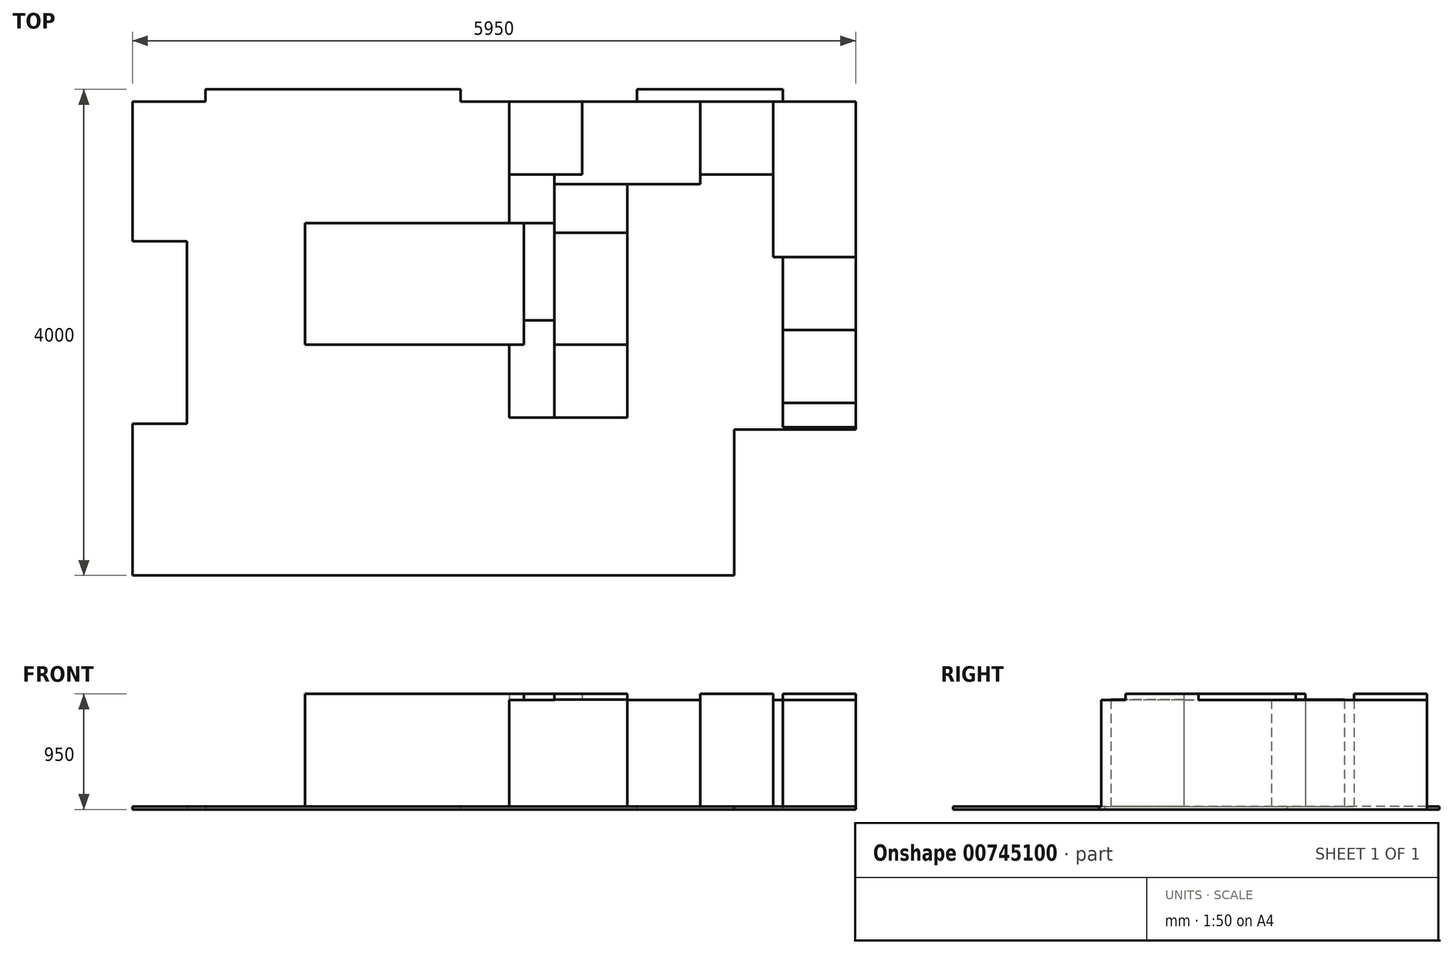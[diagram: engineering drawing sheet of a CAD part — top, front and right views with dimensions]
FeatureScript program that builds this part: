
annotation { "Feature Type Name" : "Feature", "Feature Type Description" : "" }
export const myFeature = defineFeature(function(context is Context, id is Id, definition is map)
    precondition{}
    {
        {
            var Q0;
            Q0=qCreatedBy(makeId("Top.planeOp"),FACE);
            var sketch = newSketch(context, id + "F0", { "sketchPlane" : qUnion([Q0])});
            skLineSegment(sketch, "E0.bottom", {"start": v(0, 0) * mm, "end": v(-1000, 0) * mm});
            skLineSegment(sketch, "E0.top", {"start": v(0, 2700) * mm, "end": v(-600, 2700) * mm});
            skLineSegment(sketch, "E0.left", {"start": v(0, 0) * mm, "end": v(0, 2700) * mm});
            skLineSegment(sketch, "E1.top", {"start": v(-1800, 2800) * mm, "end": v(-600, 2800) * mm});
            skLineSegment(sketch, "E1.left", {"start": v(-1800, 2700) * mm, "end": v(-1800, 2800) * mm});
            skLineSegment(sketch, "E1.right", {"start": v(-600, 2700) * mm, "end": v(-600, 2800) * mm});
            skLineSegment(sketch, "E2.top", {"start": v(-5950, -1200) * mm, "end": v(-1000, -1200) * mm});
            skLineSegment(sketch, "E2.right", {"start": v(-1000, 0) * mm, "end": v(-1000, -1200) * mm});
            skLineSegment(sketch, "E3", {"start": v(-5950, 2700) * mm, "end": v(-5950, 1550) * mm});
            skLineSegment(sketch, "E4.trimOffspring", {"start": v(-1800, 2700) * mm, "end": v(-3250, 2700) * mm});
            skLineSegment(sketch, "E5.top", {"start": v(-5350, 2800) * mm, "end": v(-3250, 2800) * mm});
            skLineSegment(sketch, "E5.left", {"start": v(-5350, 2700) * mm, "end": v(-5350, 2800) * mm});
            skLineSegment(sketch, "E5.right", {"start": v(-3250, 2700) * mm, "end": v(-3250, 2800) * mm});
            skLineSegment(sketch, "E6.trimOffspring", {"start": v(-5350, 2700) * mm, "end": v(-5950, 2700) * mm});
            skLineSegment(sketch, "E7", {"start": v(-5950, 1550) * mm, "end": v(-5500, 1550) * mm});
            skLineSegment(sketch, "E8", {"start": v(-5500, 1550) * mm, "end": v(-5500, 50) * mm});
            skLineSegment(sketch, "E9", {"start": v(-5500, 50) * mm, "end": v(-5950, 50) * mm});
            skLineSegment(sketch, "E10.trimOffspring", {"start": v(-5950, 50) * mm, "end": v(-5950, -1200) * mm});
            skSolve(sketch);
        }
        {
            var Q0;
            Q0=makeQuery(id+"F0.imprint","IMPRINT",FACE,{"disambiguationData":[TD([[makeQuery(id+"F0.imprint","IMPRINT",EDGE,{"derivedFrom":sQuery(id+"F0.wireOp",EDGE,"E0.bottom")}),-1.0]])]});
            extrude(context, id + "F1", {"entities" : qUnion([Q0]), "depth" : 25 * mm, "offsetDistance" : 25 * mm});
        }
        {
            var Q0;
            Q0=qCreatedBy(makeId("Top.planeOp"),FACE);
            var sketch = newSketch(context, id + "F2", { "sketchPlane" : qUnion([Q0])});
            skLineSegment(sketch, "E11.bottom", {"start": v(0, 2700) * mm, "end": v(-680, 2700) * mm});
            skLineSegment(sketch, "E11.top", {"start": v(0, 1420) * mm, "end": v(-680, 1420) * mm});
            skLineSegment(sketch, "E11.left", {"start": v(0, 2700) * mm, "end": v(0, 1420) * mm});
            skLineSegment(sketch, "E11.right", {"start": v(-680, 2700) * mm, "end": v(-680, 1420) * mm});
            skLineSegment(sketch, "E12.bottom", {"start": v(0, 1420) * mm, "end": v(-600, 1420) * mm});
            skLineSegment(sketch, "E12.top", {"start": v(0, 820) * mm, "end": v(-600, 820) * mm});
            skLineSegment(sketch, "E12.left", {"start": v(0, 1420) * mm, "end": v(0, 820) * mm});
            skLineSegment(sketch, "E12.right", {"start": v(-600, 1420) * mm, "end": v(-600, 820) * mm});
            skLineSegment(sketch, "E13.top", {"start": v(0, 220) * mm, "end": v(-600, 220) * mm});
            skLineSegment(sketch, "E13.left", {"start": v(0, 820) * mm, "end": v(0, 220) * mm});
            skLineSegment(sketch, "E13.right", {"start": v(-600, 820) * mm, "end": v(-600, 220) * mm});
            skLineSegment(sketch, "E14.bottom", {"start": v(-680, 2700) * mm, "end": v(-1280, 2700) * mm});
            skLineSegment(sketch, "E14.top", {"start": v(-680, 2100) * mm, "end": v(-1280, 2100) * mm});
            skLineSegment(sketch, "E14.left", {"start": v(-680, 2700) * mm, "end": v(-680, 2100) * mm});
            skLineSegment(sketch, "E14.right", {"start": v(-1280, 2700) * mm, "end": v(-1280, 2100) * mm});
            skLineSegment(sketch, "E15.bottom", {"start": v(-1280, 2700) * mm, "end": v(-2560, 2700) * mm});
            skLineSegment(sketch, "E15.top", {"start": v(-1280, 2020) * mm, "end": v(-2560, 2020) * mm});
            skLineSegment(sketch, "E15.left", {"start": v(-1280, 2700) * mm, "end": v(-1280, 2020) * mm});
            skLineSegment(sketch, "E15.right", {"start": v(-2560, 2700) * mm, "end": v(-2560, 2020) * mm});
            skLineSegment(sketch, "E16.bottom", {"start": v(-2480, 2020) * mm, "end": v(-1880, 2020) * mm});
            skLineSegment(sketch, "E16.top", {"start": v(-2480, 1620) * mm, "end": v(-1880, 1620) * mm});
            skLineSegment(sketch, "E16.left", {"start": v(-2480, 2020) * mm, "end": v(-2480, 1620) * mm});
            skLineSegment(sketch, "E16.right", {"start": v(-1880, 2020) * mm, "end": v(-1880, 1620) * mm});
            skLineSegment(sketch, "E17.top", {"start": v(-2480, 700) * mm, "end": v(-1880, 700) * mm});
            skLineSegment(sketch, "E17.left", {"start": v(-2480, 1620) * mm, "end": v(-2480, 700) * mm});
            skLineSegment(sketch, "E17.right", {"start": v(-1880, 1620) * mm, "end": v(-1880, 700) * mm});
            skLineSegment(sketch, "E18.bottom", {"start": v(-1880, 700) * mm, "end": v(-2480, 700) * mm});
            skLineSegment(sketch, "E18.top", {"start": v(-1880, 100) * mm, "end": v(-2480, 100) * mm});
            skLineSegment(sketch, "E18.left", {"start": v(-1880, 700) * mm, "end": v(-1880, 100) * mm});
            skLineSegment(sketch, "E18.right", {"start": v(-2480, 700) * mm, "end": v(-2480, 100) * mm});
            skLineSegment(sketch, "E19.bottom", {"start": v(-600, 220) * mm, "end": v(0, 220) * mm});
            skLineSegment(sketch, "E19.top", {"start": v(-600, 20) * mm, "end": v(0, 20) * mm});
            skLineSegment(sketch, "E19.left", {"start": v(-600, 220) * mm, "end": v(-600, 20) * mm});
            skLineSegment(sketch, "E19.right", {"start": v(0, 220) * mm, "end": v(0, 20) * mm});
            skLineSegment(sketch, "E20.bottom", {"start": v(-2850, 900) * mm, "end": v(-2480, 900) * mm});
            skLineSegment(sketch, "E20.top", {"start": v(-2850, 100) * mm, "end": v(-2480, 100) * mm});
            skLineSegment(sketch, "E20.left", {"start": v(-2850, 900) * mm, "end": v(-2850, 100) * mm});
            skLineSegment(sketch, "E20.right", {"start": v(-2480, 900) * mm, "end": v(-2480, 100) * mm});
            skLineSegment(sketch, "E21.top", {"start": v(-2850, 1700) * mm, "end": v(-2480, 1700) * mm});
            skLineSegment(sketch, "E21.left", {"start": v(-2850, 900) * mm, "end": v(-2850, 1700) * mm});
            skLineSegment(sketch, "E21.right", {"start": v(-2480, 900) * mm, "end": v(-2480, 1700) * mm});
            skLineSegment(sketch, "E22.bottom", {"start": v(-2250, 2700) * mm, "end": v(-2850, 2700) * mm});
            skLineSegment(sketch, "E22.top", {"start": v(-2250, 2100) * mm, "end": v(-2850, 2100) * mm});
            skLineSegment(sketch, "E22.left", {"start": v(-2250, 2700) * mm, "end": v(-2250, 2100) * mm});
            skLineSegment(sketch, "E22.right", {"start": v(-2850, 2700) * mm, "end": v(-2850, 2100) * mm});
            skLineSegment(sketch, "E23.bottom", {"start": v(-2480, 2100) * mm, "end": v(-2850, 2100) * mm});
            skLineSegment(sketch, "E23.top", {"start": v(-2480, 1700) * mm, "end": v(-2850, 1700) * mm});
            skLineSegment(sketch, "E23.left", {"start": v(-2480, 2100) * mm, "end": v(-2480, 1700) * mm});
            skLineSegment(sketch, "E23.right", {"start": v(-2850, 2100) * mm, "end": v(-2850, 1700) * mm});
            skPoint(sketch, "E24", {"position": v(-2180, 1160) * mm});
            skSolve(sketch);
        }
        {
            var Q0;
            {var subQ1=sQuery(id+"F2.wireOp",EDGE,"E16.top");Q0=makeQuery(id+"F2.imprint","IMPRINT",FACE,{"disambiguationData":[TD([[makeQuery(id+"F2.imprint","IMPRINT",EDGE,{"derivedFrom":subQ1}),1.0]])]});}
            var Q1;
            Q1=makeQuery(id+"F2.imprint","IMPRINT",FACE,{"disambiguationData":[TD([[makeQuery(id+"F2.imprint","IMPRINT",EDGE,{"derivedFrom":sQuery(id+"F2.wireOp",EDGE,"E17.top")}),-1.0]])]});
            extrude(context, id + "F3", {"entities" : qUnion([Q0, Q1]), "operationType" : NewBodyOperationType.ADD, "depth" : 903 * mm, "offsetDistance" : 25 * mm});
        }
        {
            var Q0;
            {var subQ0=sQuery(id+"F2.wireOp",EDGE,"E20.bottom");Q0=makeQuery(id+"F2.imprint","IMPRINT",FACE,{"disambiguationData":[TD([[makeQuery(id+"F2.imprint","IMPRINT",EDGE,{"derivedFrom":subQ0}),1.0]])]});}
            var Q1;
            {var subQ5=sQuery(id+"F2.wireOp",EDGE,"E11.bottom");Q1=makeQuery(id+"F2.imprint","IMPRINT",FACE,{"disambiguationData":[TD([[makeQuery(id+"F2.imprint","IMPRINT",EDGE,{"derivedFrom":subQ5}),1.0]])]});}
            var Q2;
            {var subQ5=sQuery(id+"F2.wireOp",EDGE,"E14.right");Q2=makeQuery(id+"F2.imprint","IMPRINT",FACE,{"disambiguationData":[TD([[makeQuery(id+"F2.imprint","IMPRINT",EDGE,{"derivedFrom":subQ5}),-1.0]])]});}
            var Q3;
            Q3=makeQuery(id+"F2.imprint","IMPRINT",FACE,{"disambiguationData":[TD([[makeQuery(id+"F2.imprint","IMPRINT",EDGE,{"derivedFrom":sQuery(id+"F2.wireOp",EDGE,"E13.top")}),1.0]])]});
            extrude(context, id + "F4", {"entities" : qUnion([Q0, Q1, Q2, Q3]), "operationType" : NewBodyOperationType.ADD, "depth" : 902 * mm, "offsetDistance" : 25 * mm});
        }
        {
            var Q0;
            {var subQ0=sQuery(id+"F2.wireOp",EDGE,"E21.top");Q0=makeQuery(id+"F2.imprint","IMPRINT",FACE,{"disambiguationData":[TD([[makeQuery(id+"F2.imprint","IMPRINT",EDGE,{"derivedFrom":subQ0}),1.0]])]});}
            var Q1;
            {var subQ3=sQuery(id+"F2.wireOp",EDGE,"E23.left");Q1=makeQuery(id+"F2.imprint","IMPRINT",FACE,{"disambiguationData":[TD([[makeQuery(id+"F2.imprint","IMPRINT",EDGE,{"derivedFrom":subQ3}),-1.0]])]});}
            var Q2;
            {var subQ1=sQuery(id+"F2.wireOp",EDGE,"E18.right");Q2=makeQuery(id+"F2.imprint","IMPRINT",FACE,{"disambiguationData":[TD([[makeQuery(id+"F2.imprint","IMPRINT",EDGE,{"derivedFrom":subQ1}),-1.0]])]});}
            var Q3;
            Q3=makeQuery(id+"F2.imprint","IMPRINT",FACE,{"disambiguationData":[TD([[makeQuery(id+"F2.imprint","IMPRINT",EDGE,{"derivedFrom":sQuery(id+"F2.wireOp",EDGE,"E12.top")}),-1.0]])]});
            extrude(context, id + "F5", {"entities" : qUnion([Q0, Q1, Q2, Q3]), "operationType" : NewBodyOperationType.ADD, "depth" : 901 * mm, "offsetDistance" : 25 * mm});
        }
        {
            var Q0;
            Q0=qCreatedBy(makeId("Top.planeOp"),FACE);
            var sketch = newSketch(context, id + "F6", { "sketchPlane" : qUnion([Q0])});
            skPoint(sketch, "E25", {"position": v(0, 2400) * mm});
            skPoint(sketch, "E26", {"position": v(0, 1750) * mm});
            skPoint(sketch, "E27", {"position": v(-2600, 2700) * mm});
            skPoint(sketch, "E28", {"position": v(-2000, 2700) * mm});
            skPoint(sketch, "E29", {"position": v(0, 400) * mm});
            skPoint(sketch, "E30", {"position": v(0, 1100) * mm});
            skLineSegment(sketch, "E31.bottom", {"start": v(-2037.5, 1030) * mm, "end": v(-2322.5, 1030) * mm});
            skLineSegment(sketch, "E31.top", {"start": v(-2037.5, 1300) * mm, "end": v(-2322.5, 1300) * mm});
            skLineSegment(sketch, "E31.left", {"start": v(-2037.5, 1030) * mm, "end": v(-2037.5, 1300) * mm});
            skLineSegment(sketch, "E31.right", {"start": v(-2322.5, 1030) * mm, "end": v(-2322.5, 1300) * mm});
            skPoint(sketch, "E32", {"position": v(-2180, 1165) * mm});
            skPoint(sketch, "E33", {"position": v(-3630, 1165) * mm});
            skLineSegment(sketch, "E34.bottom", {"start": v(-4530, 1700) * mm, "end": v(-2730, 1700) * mm});
            skLineSegment(sketch, "E34.top", {"start": v(-4530, 700) * mm, "end": v(-2730, 700) * mm});
            skLineSegment(sketch, "E34.left", {"start": v(-4530, 1700) * mm, "end": v(-4530, 700) * mm});
            skLineSegment(sketch, "E34.right", {"start": v(-2730, 1700) * mm, "end": v(-2730, 700) * mm});
            skSolve(sketch);
        }
        {
            var Q0;
            {var subQ0=sQuery(id+"F2.wireOp",EDGE,"E14.bottom");Q0=makeQuery(id+"F2.imprint","IMPRINT",FACE,{"disambiguationData":[TD([[makeQuery(id+"F2.imprint","IMPRINT",EDGE,{"derivedFrom":subQ0}),1.0]])]});}
            var Q1;
            Q1=makeQuery(id+"F2.imprint","IMPRINT",FACE,{"disambiguationData":[TD([[makeQuery(id+"F2.imprint","IMPRINT",EDGE,{"derivedFrom":sQuery(id+"F2.wireOp",EDGE,"E12.top")}),1.0]])]});
            var Q2;
            {var subQ3=sQuery(id+"F2.wireOp",EDGE,"E16.top");Q2=makeQuery(id+"F2.imprint","IMPRINT",FACE,{"disambiguationData":[TD([[makeQuery(id+"F2.imprint","IMPRINT",EDGE,{"derivedFrom":subQ3}),-1.0]])]});}
            var Q3;
            {var subQ0=sQuery(id+"F2.wireOp",EDGE,"E22.bottom");Q3=makeQuery(id+"F2.imprint","IMPRINT",FACE,{"disambiguationData":[TD([[makeQuery(id+"F2.imprint","IMPRINT",EDGE,{"derivedFrom":subQ0}),1.0]])]});}
            var Q4;
            {var subQ4=sQuery(id+"F2.wireOp",EDGE,"E22.left");Q4=makeQuery(id+"F2.imprint","IMPRINT",FACE,{"disambiguationData":[TD([[makeQuery(id+"F2.imprint","IMPRINT",EDGE,{"derivedFrom":subQ4}),-1.0]])]});}
            var Q5;
            Q5=makeQuery(id+"F6.imprint","IMPRINT",FACE,{"disambiguationData":[TD([[makeQuery(id+"F6.imprint","IMPRINT",EDGE,{"derivedFrom":sQuery(id+"F6.wireOp",EDGE,"E34.bottom")}),-1.0]])]});
            extrude(context, id + "F7", {"entities" : qUnion([Q0, Q1, Q2, Q3, Q4, Q5]), "operationType" : NewBodyOperationType.ADD, "depth" : 950 * mm, "offsetDistance" : 25 * mm});
        }
    });
